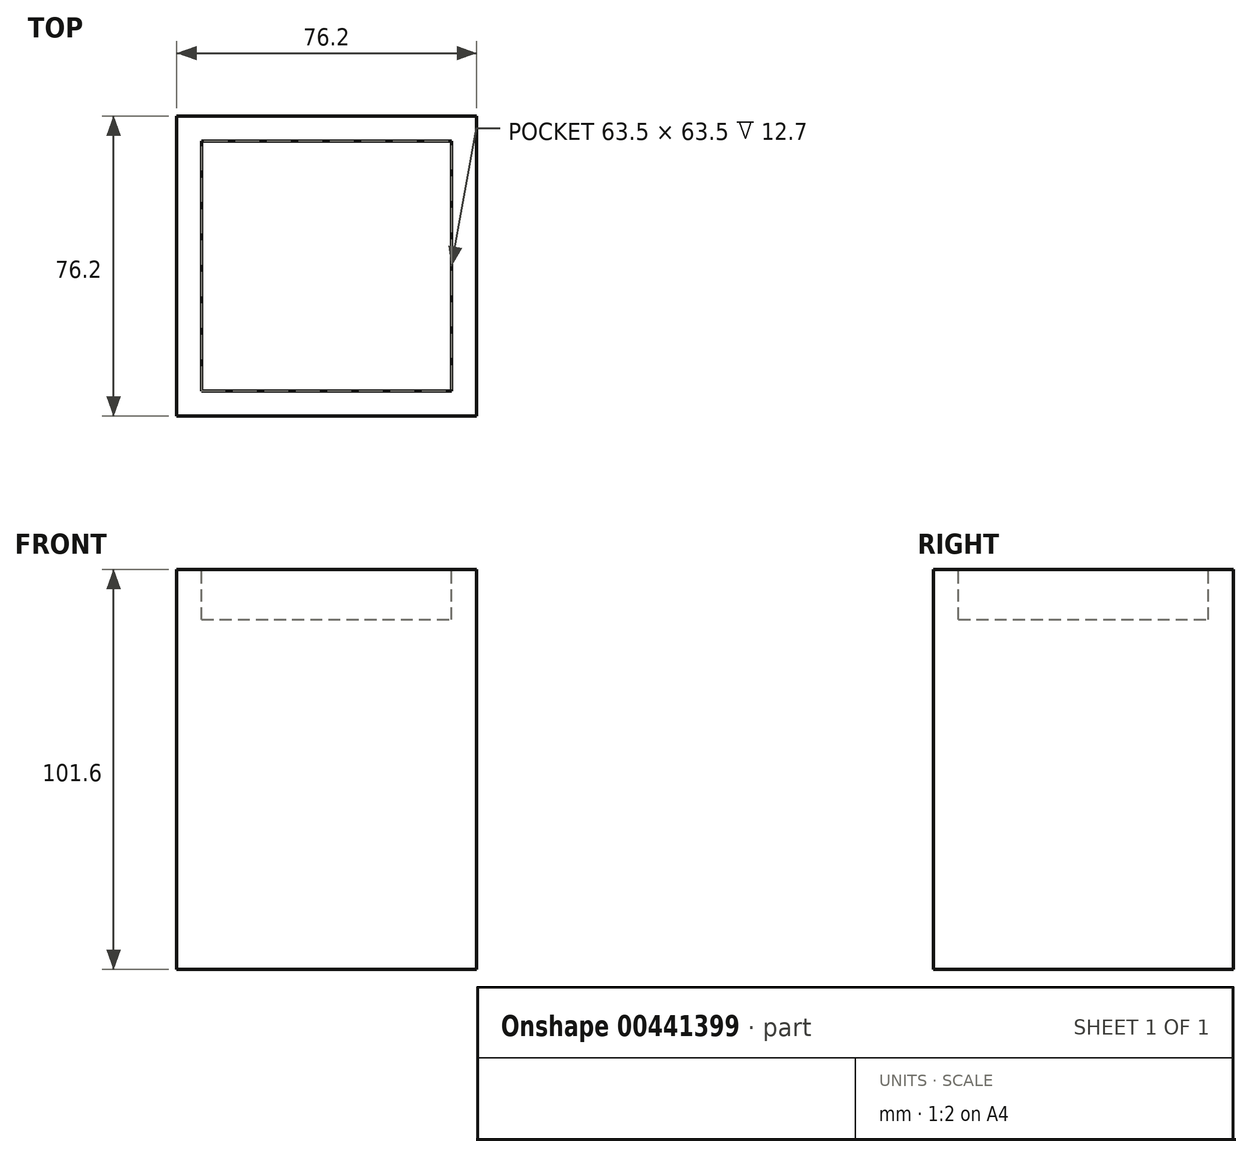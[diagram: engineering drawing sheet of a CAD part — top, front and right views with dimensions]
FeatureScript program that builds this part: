
annotation { "Feature Type Name" : "Feature", "Feature Type Description" : "" }
export const myFeature = defineFeature(function(context is Context, id is Id, definition is map)
    precondition{}
    {
        {
            var Q0;
            Q0=qCreatedBy(makeId("Top.planeOp"),FACE);
            var sketch = newSketch(context, id + "F0", { "sketchPlane" : qUnion([Q0])});
            skLineSegment(sketch, "E0.bottom", {"start": v(-35.47, -33.6) * mm, "end": v(40.73, -33.6) * mm});
            skLineSegment(sketch, "E0.top", {"start": v(-35.47, 42.6) * mm, "end": v(40.73, 42.6) * mm});
            skLineSegment(sketch, "E0.left", {"start": v(-35.47, -33.6) * mm, "end": v(-35.47, 42.6) * mm});
            skLineSegment(sketch, "E0.right", {"start": v(40.73, -33.6) * mm, "end": v(40.73, 42.6) * mm});
            skSolve(sketch);
        }
        {
            var Q0;
            Q0=makeQuery(id+"F0.imprint","IMPRINT",FACE,{"disambiguationData":[TD([[makeQuery(id+"F0.imprint","IMPRINT",EDGE,{"derivedFrom":sQuery(id+"F0.wireOp",EDGE,"E0.bottom")}),1.0]])]});
            var Q1;
            Q1 = qSketchRegion(id + "F0", true);
            extrude(context, id + "F1", {"entities" : qUnion([Q0, Q1]), "depth" : 76.2 * mm});
        }
        {
            var Q0;
            Q0=makeQuery(id+"F1.opExtrude","CAP_FACE",FACE,{"disambiguationData":[OSD([sQuery(id+"F0.wireOp",EDGE,"E0.bottom"),sQuery(id+"F0.wireOp",EDGE,"E0.top"),sQuery(id+"F0.wireOp",EDGE,"E0.left"),sQuery(id+"F0.wireOp",EDGE,"E0.right")])],"isStart":false});
            extrude(context, id + "F2", {"entities" : qUnion([Q0]), "operationType" : NewBodyOperationType.ADD, "depth" : 25.4 * mm});
        }
        {
            var Q0;
            Q0=makeQuery(id+"F2.opExtrude","CAP_FACE",FACE,{"disambiguationData":[OSD([sQuery(id+"F0.wireOp",EDGE,"E0.bottom"),sQuery(id+"F0.wireOp",EDGE,"E0.top"),sQuery(id+"F0.wireOp",EDGE,"E0.left"),sQuery(id+"F0.wireOp",EDGE,"E0.right")])],"isStart":false});
            var sketch = newSketch(context, id + "F3", { "sketchPlane" : qUnion([Q0])});
            skLineSegment(sketch, "E1.0", {"start": v(34.38, -33.6) * mm, "end": v(34.38, 42.6) * mm});
            skLineSegment(sketch, "E2.0", {"start": v(-35.47, -27.25) * mm, "end": v(40.73, -27.25) * mm});
            skLineSegment(sketch, "E3.0", {"start": v(-29.12, -33.6) * mm, "end": v(-29.12, 42.6) * mm});
            skLineSegment(sketch, "E4.0", {"start": v(-35.47, 36.25) * mm, "end": v(40.73, 36.25) * mm});
            skSolve(sketch);
        }
        {
            var Q0;
            {var subQ0=sQuery(id+"F3.wireOp",EDGE,"E2.0");var subQ1=sQuery(id+"F3.wireOp",EDGE,"E1.0");var subQ2=makeQuery(id+"F3.imprint","INTERSECT",VERTEX,{"derivedFrom":[subQ1,subQ0]});Q0=makeQuery(id+"F3.imprint","IMPRINT",FACE,{"disambiguationData":[TD([[makeQuery(id+"F3.imprint","IMPRINT",EDGE,{"disambiguationData":[TD([[subQ2,-1.0]])],"derivedFrom":subQ1}),1.0]])]});}
            extrude(context, id + "F4", {"entities" : qUnion([Q0]), "operationType" : NewBodyOperationType.REMOVE, "oppositeDirection" : true, "depth" : 12.7 * mm});
        }
    });
